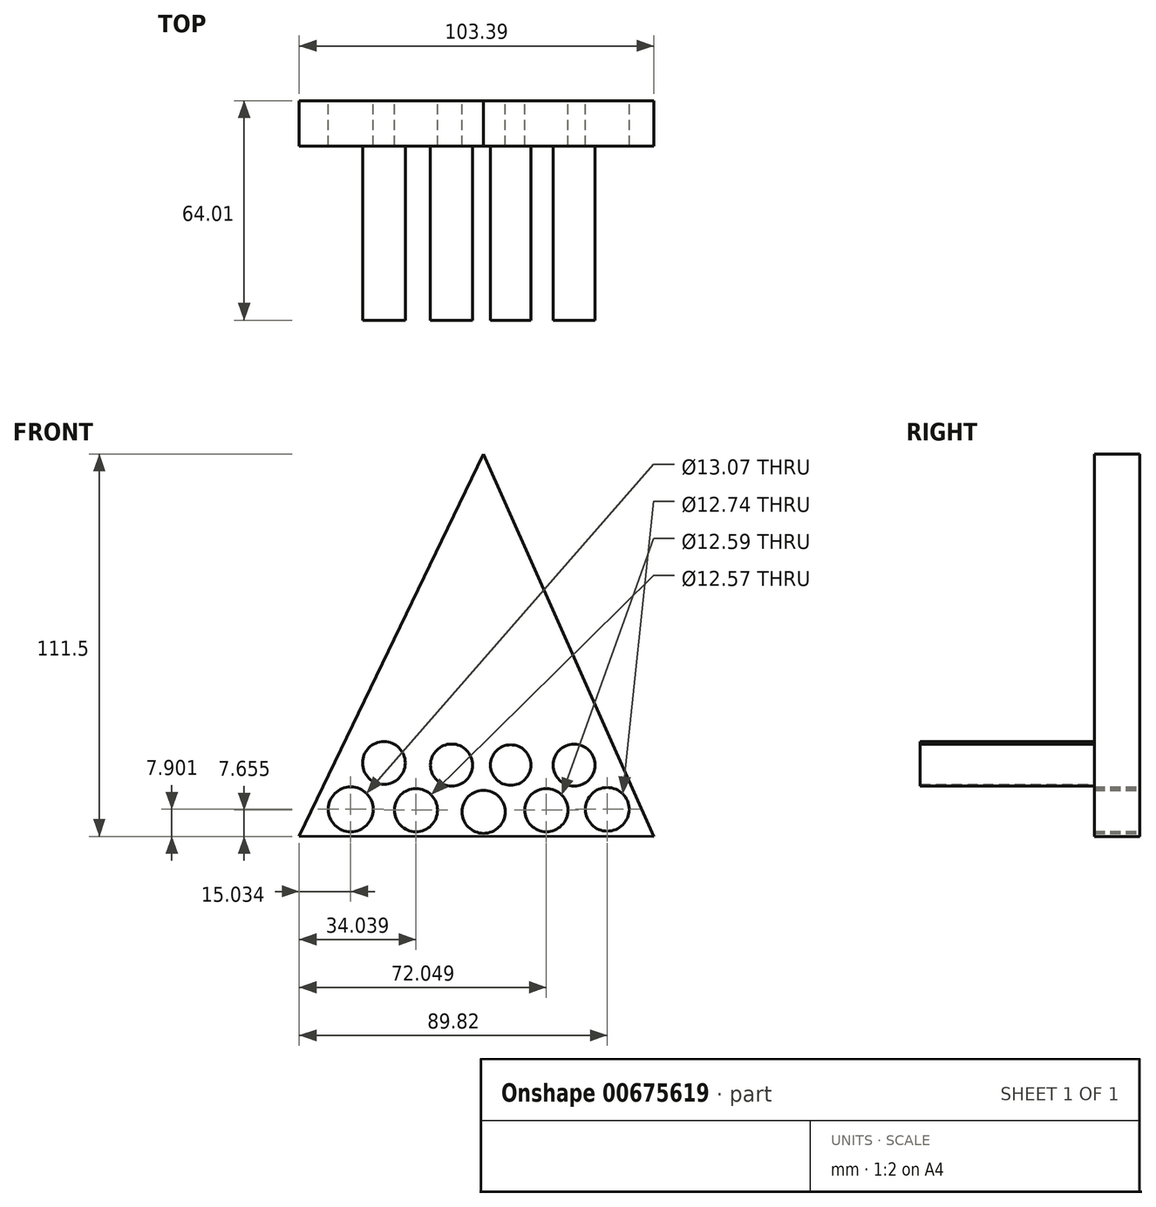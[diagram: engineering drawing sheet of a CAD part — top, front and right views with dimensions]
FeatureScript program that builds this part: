
annotation { "Feature Type Name" : "Feature", "Feature Type Description" : "" }
export const myFeature = defineFeature(function(context is Context, id is Id, definition is map)
    precondition{}
    {
        {
            var Q0;
            Q0=qCreatedBy(makeId("Front.planeOp"),FACE);
            var sketch = newSketch(context, id + "F0", { "sketchPlane" : qUnion([Q0])});
            skLineSegment(sketch, "E0", {"start": v(0, 56.04) * mm, "end": v(-53.76, -55.42) * mm});
            skLineSegment(sketch, "E1", {"start": v(0, 56.04) * mm, "end": v(49.63, -55.46) * mm});
            skLineSegment(sketch, "E2", {"start": v(49.63, -55.46) * mm, "end": v(-53.76, -55.42) * mm});
            skCircle(sketch, "E3", {"center": v(-38.73, -47.56) * mm, "radius": 6.53 * mm});
            skCircle(sketch, "E4", {"center": v(36.06, -47.56) * mm, "radius": 6.37 * mm});
            skCircle(sketch, "E5", {"center": v(0, -48.3) * mm, "radius": 6.28 * mm});
            skCircle(sketch, "E6", {"center": v(18.29, -47.8) * mm, "radius": 6.3 * mm});
            skCircle(sketch, "E7", {"center": v(-19.72, -47.8) * mm, "radius": 6.28 * mm});
            skSolve(sketch);
        }
        {
            var Q0;
            Q0 = qSketchRegion(id + "F0", true);
            extrude(context, id + "F1", {"entities" : qUnion([Q0]), "depth" : 13.2 * mm, "offsetDistance" : 25.4 * mm});
        }
        {
            var Q0;
            Q0=makeQuery(id+"F1.opExtrude","CAP_FACE",FACE,{"disambiguationData":[OSD([sQuery(id+"F0.wireOp",EDGE,"E0"),sQuery(id+"F0.wireOp",EDGE,"E1"),sQuery(id+"F0.wireOp",EDGE,"E2"),sQuery(id+"F0.wireOp",EDGE,"E3"),sQuery(id+"F0.wireOp",EDGE,"E4"),sQuery(id+"F0.wireOp",EDGE,"E5"),sQuery(id+"F0.wireOp",EDGE,"E6"),sQuery(id+"F0.wireOp",EDGE,"E7")])],"isStart":false});
            var sketch = newSketch(context, id + "F2", { "sketchPlane" : qUnion([Q0])});
            skCircle(sketch, "E8", {"center": v(-29.06, -34.04) * mm, "radius": 6.23 * mm});
            skCircle(sketch, "E9", {"center": v(-9.34, -34.66) * mm, "radius": 6.15 * mm});
            skCircle(sketch, "E10", {"center": v(7.89, -34.66) * mm, "radius": 5.9 * mm});
            skCircle(sketch, "E11", {"center": v(26.36, -34.66) * mm, "radius": 6.1 * mm});
            skSolve(sketch);
        }
        {
            var Q0;
            Q0 = qSketchRegion(id + "F2", true);
            extrude(context, id + "F3", {"entities" : qUnion([Q0]), "operationType" : NewBodyOperationType.ADD, "depth" : 50.8 * mm, "offsetDistance" : 25.4 * mm});
        }
    });
